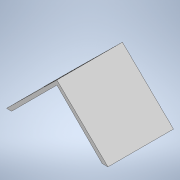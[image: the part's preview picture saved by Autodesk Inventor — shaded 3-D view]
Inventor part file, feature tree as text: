
AUTODESK INVENTOR PART (.ipt)
format: ipt  version: 2022 (Build 260153000, 153)  size: 144,384 bytes
history: native  units: mm
features: extrude x3, sketch x2, other x1, plane x1
ambient origin geometry x8: Origin, YZ Plane, XZ Plane, XY Plane, X Axis, Y Axis, Z Axis, Center Point
bodies: Body1 (feature_tree)
feature tree (7):
  other  "Sólido1"
  extrude  "Extrusión1"  Depth=196.0mm
  plane  "Plano de trabajo1"
  sketch  "Boceto3"  dims[d2=215.0mm d3=22.0mm d4=16.0mm d5=45.0deg d6=25.0mm d7=16.0mm d8=135.0deg d9=283.5mm d10=0.0mm d26=1.0mm d27=0.0mm d28=90.0mm d29=100.0mm d30=70.0mm d31=20.0mm d32=1.0mm d33=0.0mm]
  extrude  "Extrusión2"  Depth=1.0mm
  extrude  "Extrusión3"  Depth=1.0mm
  sketch  "Boceto2"  dims[d0=196.0mm d1=196.0mm]
